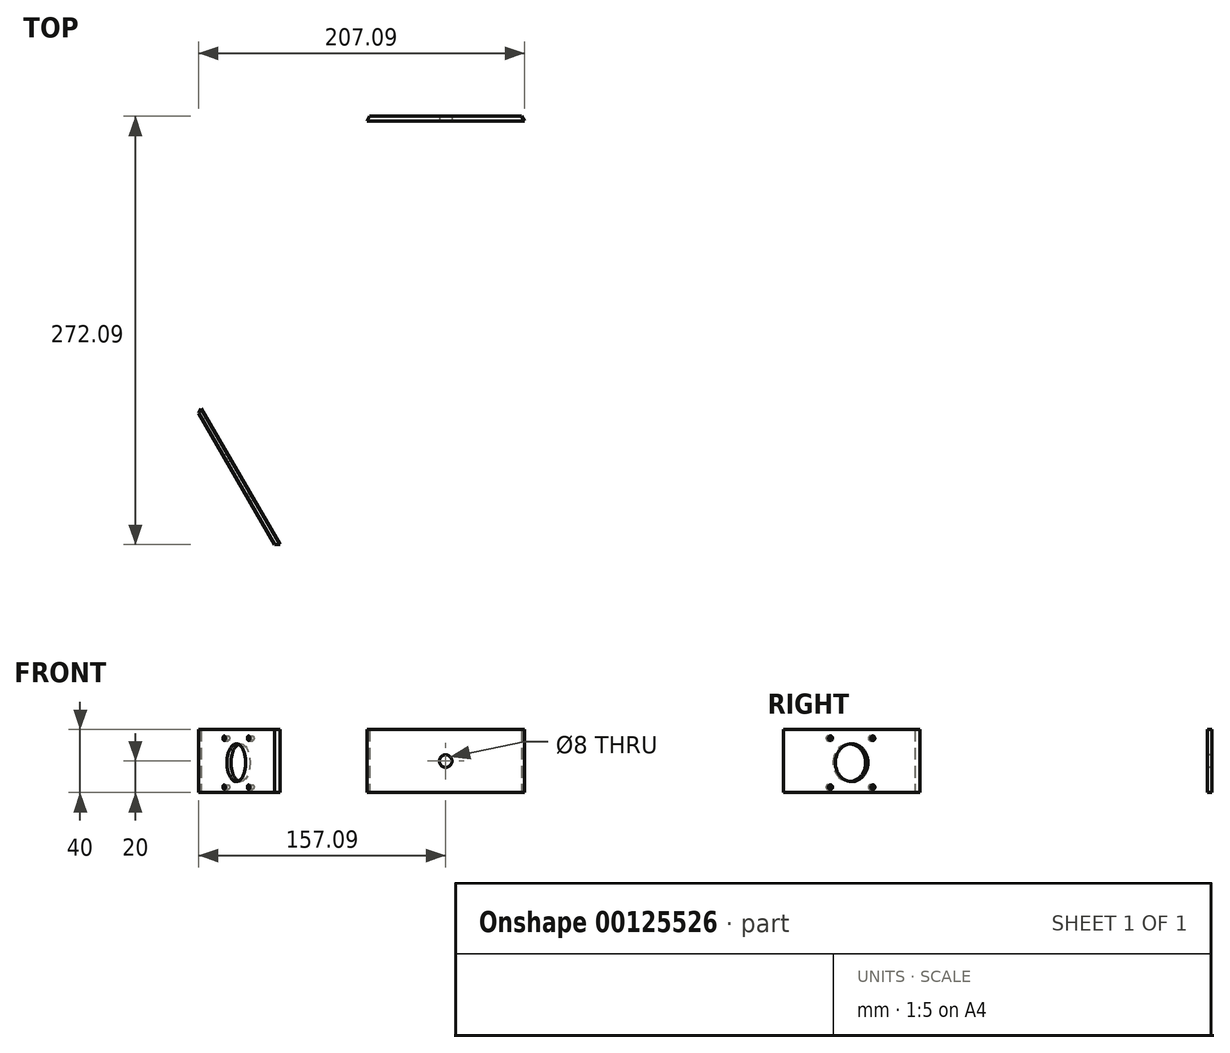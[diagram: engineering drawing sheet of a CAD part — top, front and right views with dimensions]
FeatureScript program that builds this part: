
annotation { "Feature Type Name" : "Feature", "Feature Type Description" : "" }
export const myFeature = defineFeature(function(context is Context, id is Id, definition is map)
    precondition{}
    {
        {
            var Q0;
            Q0=qCreatedBy(makeId("Top.planeOp"),FACE);
            var sketch = newSketch(context, id + "F0", { "sketchPlane" : qUnion([Q0])});
            skLineSegment(sketch, "E0", {"start": v(-200, -138.56) * mm, "end": v(200, -138.56) * mm});
            skLineSegment(sketch, "E1", {"start": v(200, -138.56) * mm, "end": v(220, -103.92) * mm});
            skLineSegment(sketch, "E2", {"start": v(220, -103.92) * mm, "end": v(20, 242.49) * mm});
            skLineSegment(sketch, "E3", {"start": v(20, 242.49) * mm, "end": v(-20, 242.49) * mm});
            skLineSegment(sketch, "E4", {"start": v(-20, 242.49) * mm, "end": v(-220, -103.92) * mm});
            skLineSegment(sketch, "E5", {"start": v(-220, -103.92) * mm, "end": v(-200, -138.56) * mm});
            skLineSegment(sketch, "E6", {"start": v(0, 242.49) * mm, "end": v(0, -138.56) * mm, "construction": true});
            skLineSegment(sketch, "E7", {"start": v(-120, 69.28) * mm, "end": v(210, -121.24) * mm, "construction": true});
            skPoint(sketch, "E8", {"position": v(0, 0) * mm});
            skCircle(sketch, "E9", {"center": v(0, 0) * mm, "radius": 138.56 * mm, "construction": true});
            skLineSegment(sketch, "E10", {"start": v(-220, -103.92) * mm, "end": v(-185.36, -83.92) * mm});
            skLineSegment(sketch, "E11", {"start": v(-185.36, -83.92) * mm, "end": v(-165.36, -118.56) * mm});
            skLineSegment(sketch, "E12", {"start": v(-165.36, -118.56) * mm, "end": v(-200, -138.56) * mm});
            skLineSegment(sketch, "E13", {"start": v(-20, 242.49) * mm, "end": v(-20, 202.49) * mm});
            skLineSegment(sketch, "E14", {"start": v(-20, 202.49) * mm, "end": v(20, 202.49) * mm});
            skLineSegment(sketch, "E15", {"start": v(20, 202.49) * mm, "end": v(20, 242.49) * mm});
            skLineSegment(sketch, "E16", {"start": v(220, -103.92) * mm, "end": v(185.36, -83.92) * mm});
            skLineSegment(sketch, "E17", {"start": v(185.36, -83.92) * mm, "end": v(165.36, -118.56) * mm});
            skLineSegment(sketch, "E18", {"start": v(165.36, -118.56) * mm, "end": v(200, -138.56) * mm});
            skLineSegment(sketch, "E19", {"start": v(-185.36, -83.92) * mm, "end": v(-20, 202.49) * mm});
            skLineSegment(sketch, "E20", {"start": v(20, 202.49) * mm, "end": v(185.36, -83.92) * mm});
            skLineSegment(sketch, "E21", {"start": v(165.36, -118.56) * mm, "end": v(-165.36, -118.56) * mm});
            skCircle(sketch, "E22", {"center": v(0, 0) * mm, "radius": 110 * mm});
            skSolve(sketch);
        }
        {
            var Q0;
            Q0=makeQuery(id+"F0.imprint","IMPRINT",FACE,{"disambiguationData":[TD([[makeQuery(id+"F0.imprint","IMPRINT",EDGE,{"derivedFrom":sQuery(id+"F0.wireOp",EDGE,"E22")}),1.0]])]});
            var sketch = newSketch(context, id + "F1", { "sketchPlane" : qUnion([Q0])});
            skLineSegment(sketch, "E23.0", {"start": v(-185.36, -83.92) * mm, "end": v(-20, 202.49) * mm});
            skLineSegment(sketch, "E23.1", {"start": v(20, 202.49) * mm, "end": v(185.36, -83.92) * mm});
            skLineSegment(sketch, "E23.2", {"start": v(165.36, -118.56) * mm, "end": v(-165.36, -118.56) * mm});
            skLineSegment(sketch, "E24", {"start": v(-157.1, -34.96) * mm, "end": v(-108.82, -118.56) * mm});
            skLineSegment(sketch, "E25", {"start": v(-48.27, 153.53) * mm, "end": v(48.27, 153.53) * mm});
            skLineSegment(sketch, "E26", {"start": v(-50, 150.53) * mm, "end": v(50, 150.53) * mm});
            skLineSegment(sketch, "E27", {"start": v(-155.36, -31.96) * mm, "end": v(-105.36, -118.56) * mm});
            skSolve(sketch);
        }
        {
            var Q0;
            {var subQ1=sQuery(id+"F1.wireOp",EDGE,"E24");Q0=makeQuery(id+"F1.imprint","IMPRINT",FACE,{"disambiguationData":[TD([[makeQuery(id+"F1.imprint","IMPRINT",EDGE,{"derivedFrom":subQ1}),1.0]])]});}
            var Q1;
            {var subQ0=sQuery(id+"F1.wireOp",EDGE,"E25");Q1=makeQuery(id+"F1.imprint","IMPRINT",FACE,{"disambiguationData":[TD([[makeQuery(id+"F1.imprint","IMPRINT",EDGE,{"derivedFrom":subQ0}),-1.0]])]});}
            extrude(context, id + "F2", {"entities" : qUnion([Q0, Q1]), "depth" : 40 * mm});
        }
        {
            var Q0;
            Q0=makeQuery(id+"F2.opExtrude","SWEPT_FACE",FACE,{"disambiguationData":[OSD([sQuery(id+"F1.wireOp",EDGE,"E27")])]});
            var sketch = newSketch(context, id + "F3", { "sketchPlane" : qUnion([Q0])});
            skCircle(sketch, "E28", {"center": v(0, 19) * mm, "radius": 12 * mm});
            skLineSegment(sketch, "E29.bottom", {"start": v(-15.5, 34.5) * mm, "end": v(15.5, 34.5) * mm, "construction": true});
            skLineSegment(sketch, "E29.top", {"start": v(-15.5, 3.5) * mm, "end": v(15.5, 3.5) * mm, "construction": true});
            skLineSegment(sketch, "E29.left", {"start": v(-15.5, 34.5) * mm, "end": v(-15.5, 3.5) * mm, "construction": true});
            skLineSegment(sketch, "E29.right", {"start": v(15.5, 34.5) * mm, "end": v(15.5, 3.5) * mm, "construction": true});
            skCircle(sketch, "E30", {"center": v(-15.5, 34.5) * mm, "radius": 1.5 * mm});
            skCircle(sketch, "E31", {"center": v(15.5, 34.5) * mm, "radius": 1.5 * mm});
            skCircle(sketch, "E32", {"center": v(15.5, 3.5) * mm, "radius": 1.5 * mm});
            skCircle(sketch, "E33", {"center": v(-15.5, 3.5) * mm, "radius": 1.5 * mm});
            skLineSegment(sketch, "E34", {"start": v(0, 19) * mm, "end": v(0, 0) * mm, "construction": true});
            skSolve(sketch);
        }
        {
            var Q0;
            Q0 = qSketchRegion(id + "F3", true);
            extrude(context, id + "F4", {"entities" : qUnion([Q0]), "operationType" : NewBodyOperationType.REMOVE, "oppositeDirection" : true, "depth" : 25 * mm});
        }
        {
            var Q0;
            Q0=makeQuery(id+"F2.opExtrude","SWEPT_FACE",FACE,{"disambiguationData":[OSD([sQuery(id+"F1.wireOp",EDGE,"E26")])]});
            var sketch = newSketch(context, id + "F5", { "sketchPlane" : qUnion([Q0])});
            skCircle(sketch, "E35", {"center": v(0, 20) * mm, "radius": 4 * mm});
            skPoint(sketch, "E35.centerSnap0", {"position": v(0, 0) * mm});
            skSolve(sketch);
        }
        {
            var Q0;
            Q0=makeQuery(id+"F5.imprint","IMPRINT",FACE,{"disambiguationData":[TD([[makeQuery(id+"F5.imprint","IMPRINT",EDGE,{"derivedFrom":sQuery(id+"F5.wireOp",EDGE,"E35")}),1.0]])]});
            extrude(context, id + "F6", {"entities" : qUnion([Q0]), "operationType" : NewBodyOperationType.REMOVE, "oppositeDirection" : true, "depth" : 25 * mm});
        }
    });
